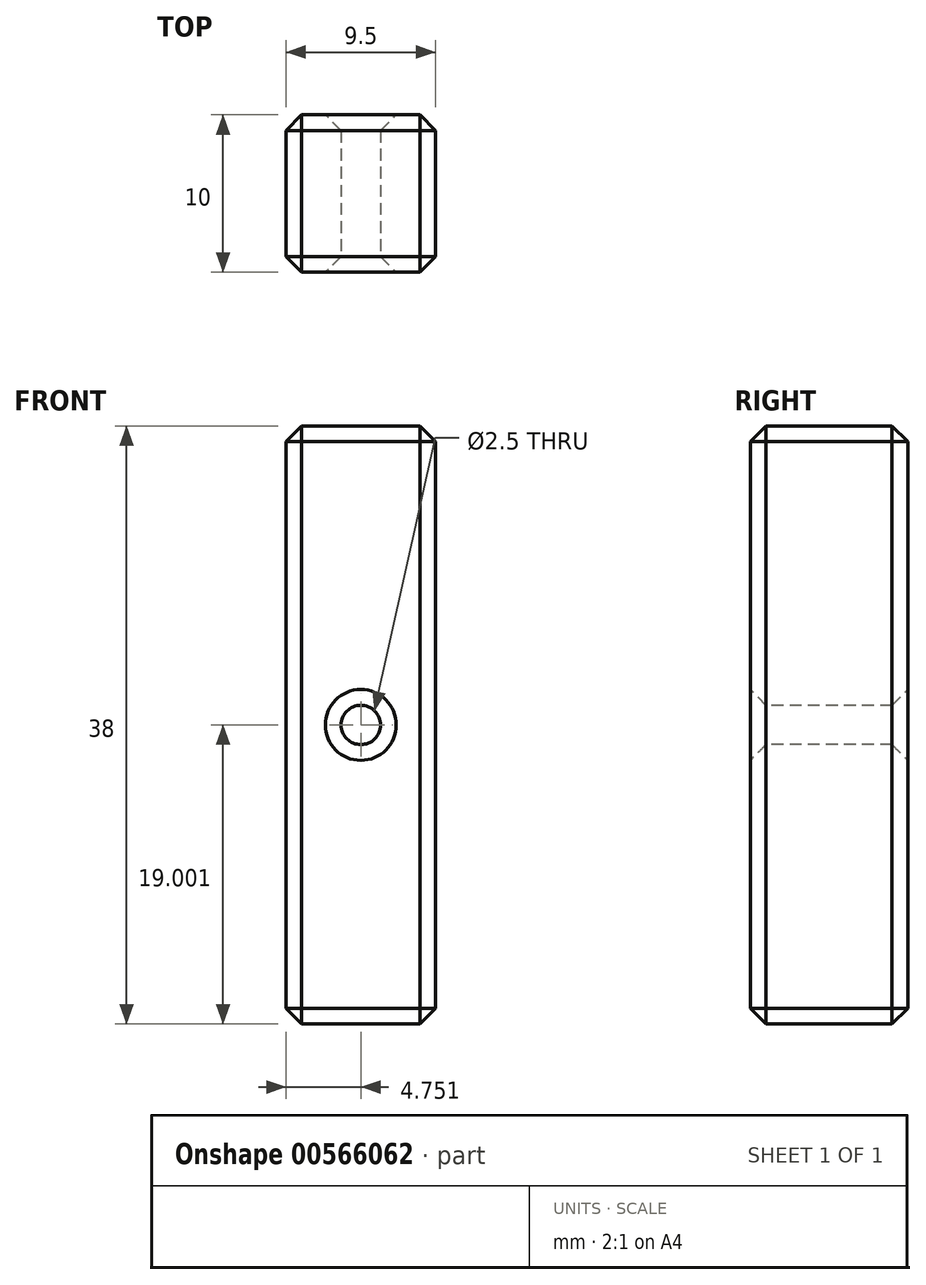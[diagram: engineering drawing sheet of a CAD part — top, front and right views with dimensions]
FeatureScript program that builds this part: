
annotation { "Feature Type Name" : "Feature", "Feature Type Description" : "" }
export const myFeature = defineFeature(function(context is Context, id is Id, definition is map)
    precondition{}
    {
        {
            var Q0;
            Q0=qCreatedBy(makeId("Front.planeOp"),FACE);
            var sketch = newSketch(context, id + "F0", { "sketchPlane" : qUnion([Q0])});
            skLineSegment(sketch, "E0.bottom", {"start": v(-26.62, 35.62) * mm, "end": v(-17.12, 35.62) * mm});
            skLineSegment(sketch, "E0.top", {"start": v(-26.62, -2.38) * mm, "end": v(-17.12, -2.38) * mm});
            skLineSegment(sketch, "E0.left", {"start": v(-26.62, 35.62) * mm, "end": v(-26.62, -2.38) * mm});
            skLineSegment(sketch, "E0.right", {"start": v(-17.12, 35.62) * mm, "end": v(-17.12, -2.38) * mm});
            skSolve(sketch);
        }
        {
            var Q0;
            Q0=makeQuery(id+"F0.imprint","IMPRINT",FACE,{"disambiguationData":[TD([[makeQuery(id+"F0.imprint","IMPRINT",EDGE,{"derivedFrom":sQuery(id+"F0.wireOp",EDGE,"E0.bottom")}),-1.0]])]});
            extrude(context, id + "F1", {"entities" : qUnion([Q0]), "depth" : 10 * mm, "offsetDistance" : 25 * mm});
        }
        {
            var Q0;
            Q0=makeQuery(id+"F1.opExtrude","CAP_FACE",FACE,{"disambiguationData":[OSD([sQuery(id+"F0.wireOp",EDGE,"E0.bottom"),sQuery(id+"F0.wireOp",EDGE,"E0.top"),sQuery(id+"F0.wireOp",EDGE,"E0.left"),sQuery(id+"F0.wireOp",EDGE,"E0.right")])],"isStart":false});
            var sketch = newSketch(context, id + "F2", { "sketchPlane" : qUnion([Q0])});
            skCircle(sketch, "E1", {"center": v(-21.87, 16.62) * mm, "radius": 1.25 * mm});
            skPoint(sketch, "E1.centerSnap0", {"position": v(-26.62, 16.62) * mm});
            skPoint(sketch, "E1.centerSnap1", {"position": v(-21.87, 35.62) * mm});
            skSolve(sketch);
        }
        {
            var Q0;
            Q0=makeQuery(id+"F2.imprint","IMPRINT",FACE,{"disambiguationData":[TD([[makeQuery(id+"F2.imprint","IMPRINT",EDGE,{"derivedFrom":sQuery(id+"F2.wireOp",EDGE,"E1")}),1.0]])]});
            extrude(context, id + "F3", {"entities" : qUnion([Q0]), "operationType" : NewBodyOperationType.REMOVE, "oppositeDirection" : true, "depth" : 25 * mm, "offsetDistance" : 25 * mm});
        }
        {
            var Q0;
            Q0=makeQuery(id+"F1.opExtrude","CAP_FACE",FACE,{"disambiguationData":[OSD([sQuery(id+"F0.wireOp",EDGE,"E0.bottom"),sQuery(id+"F0.wireOp",EDGE,"E0.top"),sQuery(id+"F0.wireOp",EDGE,"E0.left"),sQuery(id+"F0.wireOp",EDGE,"E0.right")])],"isStart":false});
            var Q1;
            Q1=makeQuery(id+"F1.opExtrude","CAP_FACE",FACE,{"disambiguationData":[OSD([sQuery(id+"F0.wireOp",EDGE,"E0.bottom"),sQuery(id+"F0.wireOp",EDGE,"E0.top"),sQuery(id+"F0.wireOp",EDGE,"E0.left"),sQuery(id+"F0.wireOp",EDGE,"E0.right")])],"isStart":true});
            var Q2;
            Q2=makeQuery(id+"F1.opExtrude","SWEPT_FACE",FACE,{"disambiguationData":[OSD([sQuery(id+"F0.wireOp",EDGE,"E0.left")])]});
            var Q3;
            Q3=makeQuery(id+"F1.opExtrude","SWEPT_FACE",FACE,{"disambiguationData":[OSD([sQuery(id+"F0.wireOp",EDGE,"E0.right")])]});
            chamfer(context, id + "F4", {"entities" : qUnion([Q0, Q1, Q2, Q3]), "width" : 1 * mm, "tangentPropagation" : true});
        }
    });
